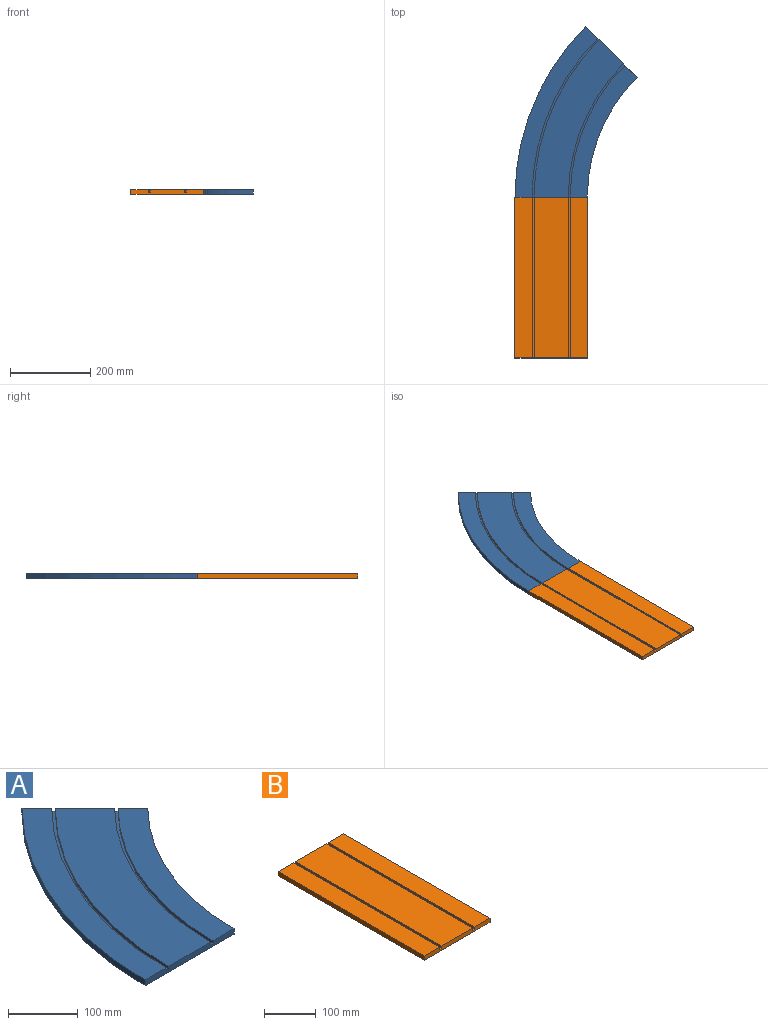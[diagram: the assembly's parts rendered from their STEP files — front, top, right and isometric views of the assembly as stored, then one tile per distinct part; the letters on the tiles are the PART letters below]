
ASSEMBLY  parts=2 mates=1
PART A: 14 faces, bbox 303.4x425.2x10 mm
  f0: plane 395.18x167.22mm, normal (0,0,1), area 2184.9mm2, adj f1,f11,f12,f13
  f1: cylinder r=558.87mm len=395.18mm, axis (0,0,1), area 2194.7mm2, adj f0,f2,f12,f13
  f2: plane 425.23x206.19mm, normal (0,0,1), area 19364.1mm2, adj f1,f3,f12,f13
  f3: cylinder r=601.37mm len=425.23mm, axis (0,0,1), area 4723.1mm2, adj f2,f4,f12,f13
  f4: plane 425.23x303.42mm, normal (0,0,-1), area 72293.2mm2, adj f3,f5,f12,f13
  f5: cylinder r=421.37mm len=297.95mm, axis (0,0,1), area 3309.4mm2, adj f4,f6,f12,f13
  f6: plane 328.01x165.92mm, normal (0,0,1), area 14774.4mm2, adj f5,f7,f12,f13
  f7: cylinder r=463.87mm len=328.01mm, axis (0,0,1), area 1821.6mm2, adj f6,f8,f12,f13
  f8: plane 331.54x140.86mm, normal (0,0,1), area 1831.4mm2, adj f7,f9,f12,f13
  f9: cylinder r=468.87mm len=331.54mm, axis (0,0,1), area 1841.2mm2, adj f8,f10,f12,f13
  f10: plane 391.65x222.33mm, normal (0,0,1), area 34138.5mm2, adj f9,f11,f12,f13
  f11: cylinder r=553.87mm len=391.65mm, axis (0,0,1), area 2175mm2, adj f0,f10,f12,f13
  f12: plane 127.28x127.28mm, normal (0.71,0.71,0), area 1750mm2, adj f0,f1,f2,f3,f4,f5,f6,f7
  f13: plane 180x10mm, normal (0,-1,0), area 1750mm2, adj f0,f1,f2,f3,f4,f5,f6,f7
PART B: 14 faces, bbox 180x400x10 mm
  f0: plane 400x5mm, normal (0,0,1), area 2000mm2, adj f1,f11,f12,f13
  f1: plane 400x5mm, normal (1,0,0), area 2000mm2, adj f0,f2,f12,f13
  f2: plane 400x42.5mm, normal (0,0,1), area 17000mm2, adj f1,f3,f12,f13
  f3: plane 400x10mm, normal (-1,0,0), area 4000mm2, adj f2,f4,f12,f13
  f4: plane 400x180mm, normal (0,0,-1), area 72000mm2, adj f3,f5,f12,f13
  f5: plane 400x10mm, normal (1,0,0), area 4000mm2, adj f4,f6,f12,f13
  f6: plane 400x42.5mm, normal (0,0,1), area 17000mm2, adj f5,f7,f12,f13
  f7: plane 400x5mm, normal (-1,0,0), area 2000mm2, adj f6,f8,f12,f13
  f8: plane 400x5mm, normal (0,0,1), area 2000mm2, adj f7,f9,f12,f13
  f9: plane 400x5mm, normal (1,0,0), area 2000mm2, adj f8,f10,f12,f13
  f10: plane 400x85mm, normal (0,0,1), area 34000mm2, adj f9,f11,f12,f13
  f11: plane 400x5mm, normal (-1,0,0), area 2000mm2, adj f0,f10,f12,f13
  f12: plane 180x10mm, normal (0,1,0), area 1750mm2, adj f0,f1,f2,f3,f4,f5,f6,f7
  f13: plane 180x10mm, normal (0,-1,0), area 1750mm2, adj f0,f1,f2,f3,f4,f5,f6,f7
PLACE A t=(-80.83,155.92,5.31)mm
PLACE B t=(-80.83,-44.08,3.88)mm fixed
MATE pin_slot A.f6 <-> B.f6  axis (0,0,1) through (9.17,155.92,8.88)mm
